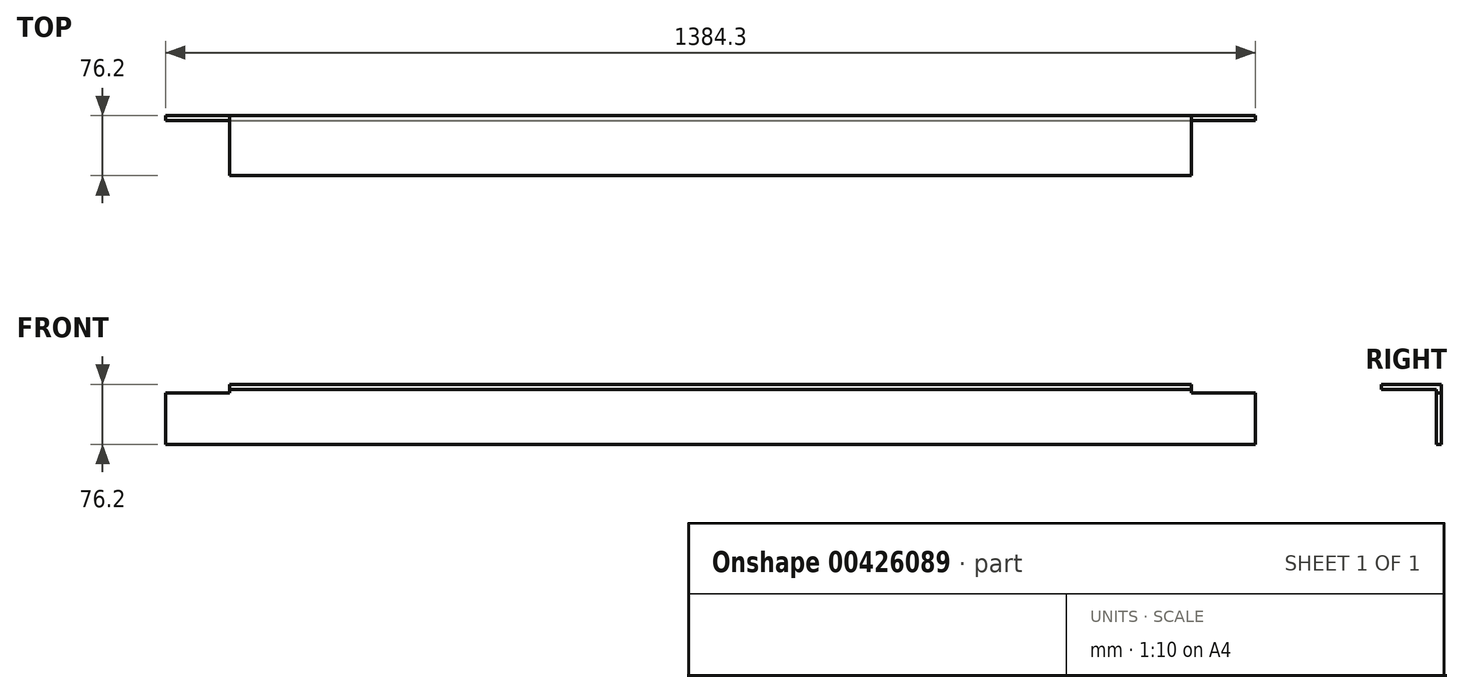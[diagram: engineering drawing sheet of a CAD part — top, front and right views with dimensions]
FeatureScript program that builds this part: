
annotation { "Feature Type Name" : "Feature", "Feature Type Description" : "" }
export const myFeature = defineFeature(function(context is Context, id is Id, definition is map)
    precondition{}
    {
        {
            var Q0;
            Q0=qCreatedBy(makeId("Front.planeOp"),FACE);
            var sketch = newSketch(context, id + "F0", { "sketchPlane" : qUnion([Q0])});
            skLineSegment(sketch, "E0.top", {"start": v(-692.15, -38.1) * mm, "end": v(692.15, -38.1) * mm});
            skPoint(sketch, "E0.middle", {"position": v(0, 0) * mm});
            skLineSegment(sketch, "E1", {"start": v(-692.15, 26.92) * mm, "end": v(-611.12, 26.92) * mm});
            skLineSegment(sketch, "E2", {"start": v(-611.12, 26.92) * mm, "end": v(-611.12, 38.1) * mm});
            skLineSegment(sketch, "E3", {"start": v(611.12, 38.1) * mm, "end": v(611.12, 26.92) * mm});
            skLineSegment(sketch, "E4", {"start": v(611.12, 26.92) * mm, "end": v(692.15, 26.92) * mm});
            skLineSegment(sketch, "E5", {"start": v(692.15, -38.1) * mm, "end": v(692.15, 26.92) * mm});
            skLineSegment(sketch, "E6", {"start": v(-611.12, 38.1) * mm, "end": v(611.12, 38.1) * mm});
            skLineSegment(sketch, "E7", {"start": v(-692.15, -38.1) * mm, "end": v(-692.15, 26.92) * mm});
            skSolve(sketch);
        }
        {
            var Q0;
            Q0=makeQuery(id+"F0.imprint","IMPRINT",FACE,{"disambiguationData":[TD([[makeQuery(id+"F0.imprint","IMPRINT",EDGE,{"derivedFrom":sQuery(id+"F0.wireOp",EDGE,"E0.top")}),1.0]])]});
            extrude(context, id + "F1", {"entities" : qUnion([Q0]), "depth" : 6.35 * mm});
        }
        {
            var Q0;
            Q0=makeQuery(id+"F1.opExtrude","CAP_FACE",FACE,{"disambiguationData":[OSD([sQuery(id+"F0.wireOp",EDGE,"E0.top"),sQuery(id+"F0.wireOp",EDGE,"E1"),sQuery(id+"F0.wireOp",EDGE,"E2"),sQuery(id+"F0.wireOp",EDGE,"E3"),sQuery(id+"F0.wireOp",EDGE,"E4"),sQuery(id+"F0.wireOp",EDGE,"E5"),sQuery(id+"F0.wireOp",EDGE,"E6"),sQuery(id+"F0.wireOp",EDGE,"E7")])],"isStart":false});
            var sketch = newSketch(context, id + "F2", { "sketchPlane" : qUnion([Q0])});
            skLineSegment(sketch, "E8", {"start": v(-611.12, 31.75) * mm, "end": v(611.12, 31.75) * mm});
            skSolve(sketch);
        }
        {
            var Q0;
            {var subQ0=sQuery(id+"F2.wireOp",EDGE,"E8");Q0=makeQuery(id+"F2.imprint","IMPRINT",FACE,{"disambiguationData":[TD([[makeQuery(id+"F2.imprint","IMPRINT",EDGE,{"derivedFrom":subQ0}),1.0]])]});}
            extrude(context, id + "F3", {"entities" : qUnion([Q0]), "operationType" : NewBodyOperationType.ADD, "depth" : 69.85 * mm});
        }
    });
